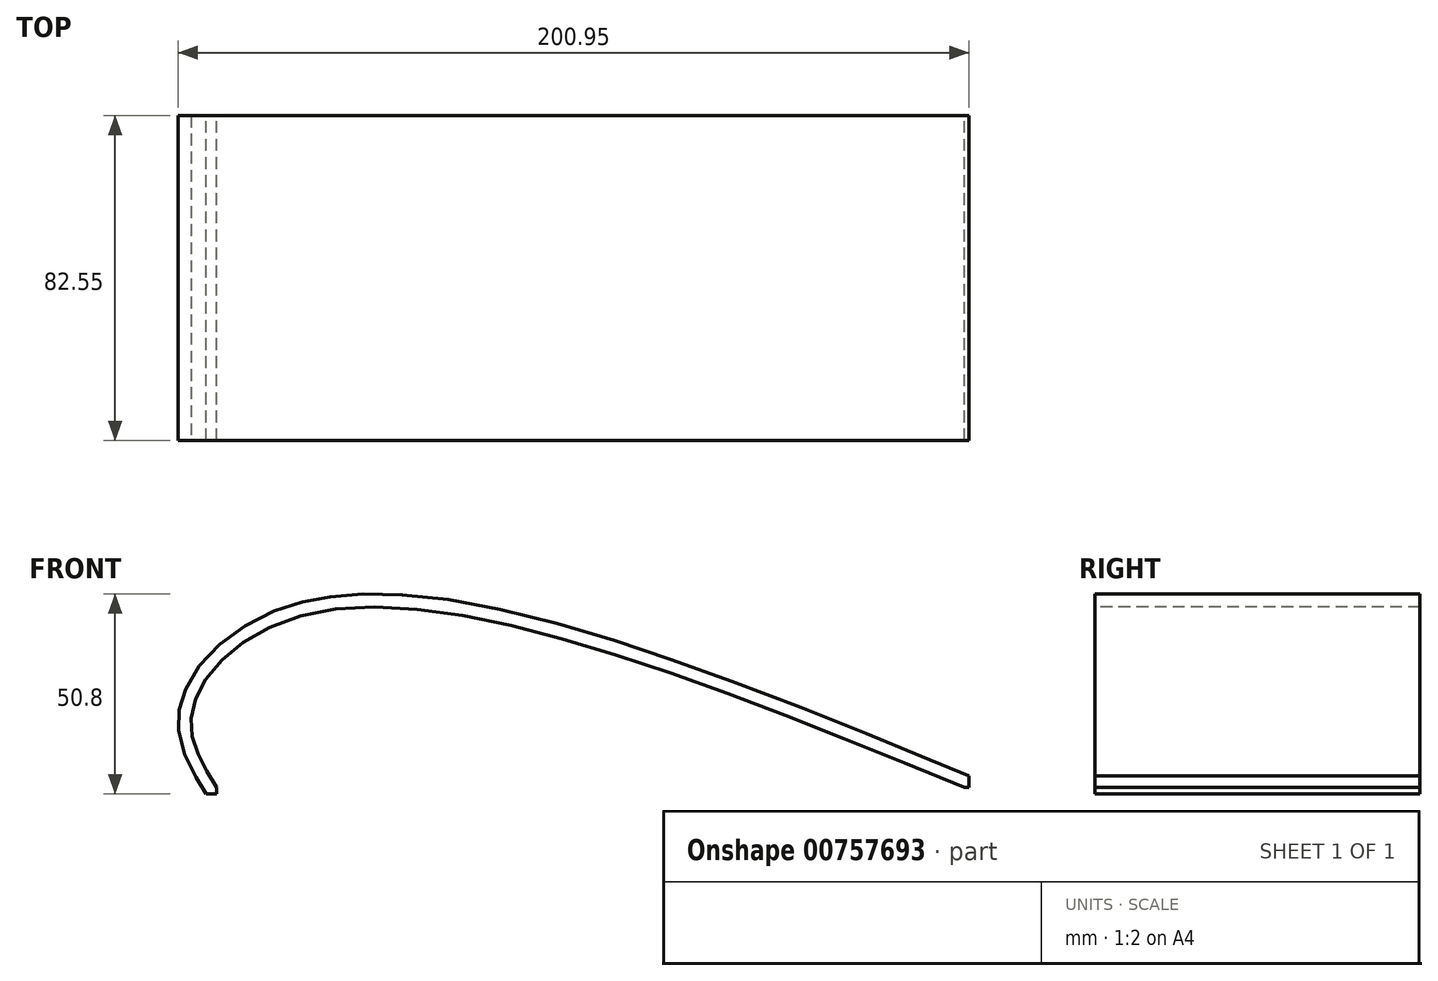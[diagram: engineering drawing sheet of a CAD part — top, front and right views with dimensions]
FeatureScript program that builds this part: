
annotation { "Feature Type Name" : "Feature", "Feature Type Description" : "" }
export const myFeature = defineFeature(function(context is Context, id is Id, definition is map)
    precondition{}
    {
        {
            var Q0;
            Q0=qCreatedBy(makeId("Front.planeOp"),FACE);
            var sketch = newSketch(context, id + "F0", { "sketchPlane" : qUnion([Q0])});
            skFitSpline(sketch, "E0", {"points": [v(63.7, -23.12) * mm, v(-101.4, 21.33) * mm, v(-132.6, -4.07) * mm, v(-126.25, -23.12) * mm], "startDerivative": vector(-351.2, 143.2) * mm, "endDerivative": vector(60.25, -96.6) * mm});
            skFitSpline(sketch, "E1.0", {"points": [v(64.9, -20.18) * mm, v(50.27, -14.2) * mm, v(28.3, -5.25) * mm, v(-0.09, 5.5) * mm, v(-20.69, 12.67) * mm, v(-40.36, 18.63) * mm, v(-58.9, 23.09) * mm, v(-73.21, 25.28) * mm, v(-83.9, 25.96) * mm, v(-91.5, 25.89) * mm, v(-97.47, 25.3) * mm, v(-102.02, 24.48) * mm, v(-106.4, 23.43) * mm, v(-111.54, 21.7) * mm, v(-117.1, 19.06) * mm, v(-122.03, 15.96) * mm, v(-126.29, 12.49) * mm, v(-129.85, 8.72) * mm, v(-132.67, 4.76) * mm, v(-134.37, 1.33) * mm, v(-135.3, -1.44) * mm, v(-135.78, -3.54) * mm, v(-136, -5.62) * mm, v(-136.01, -8.32) * mm, v(-135.5, -11.56) * mm, v(-134.3, -15.17) * mm, v(-132.69, -18.55) * mm, v(-130.85, -21.74) * mm, v(-129.58, -23.79) * mm, v(-128.95, -24.8) * mm]});
            skLineSegment(sketch, "E2", {"start": v(-128.95, -24.8) * mm, "end": v(-126.25, -24.8) * mm});
            skLineSegment(sketch, "E3", {"start": v(-126.25, -23.12) * mm, "end": v(-126.25, -24.8) * mm});
            skLineSegment(sketch, "E4", {"start": v(64.9, -20.18) * mm, "end": v(64.9, -23.12) * mm});
            skLineSegment(sketch, "E5", {"start": v(63.7, -23.12) * mm, "end": v(64.9, -23.12) * mm});
            skSolve(sketch);
        }
        {
            var Q0;
            Q0 = qSketchRegion(id + "F0", true);
            extrude(context, id + "F1", {"entities" : qUnion([Q0]), "depth" : 82.55 * mm, "offsetDistance" : 25.4 * mm});
        }
    });
